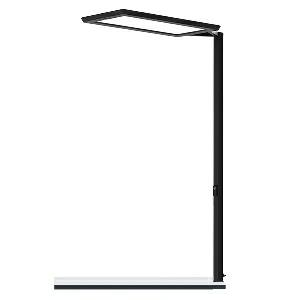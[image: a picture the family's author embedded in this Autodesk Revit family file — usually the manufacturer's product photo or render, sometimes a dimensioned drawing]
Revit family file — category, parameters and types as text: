
# Revit family: yara_single_-_yat_12000_840_r_sw_cee_00_00810197_816a
name_source: partatom
category: Lighting Fixtures
units: mm (PartAtom-declared; Revit-internal decimal feet)

## family parameters
Cut with Voids When Loaded = No
Host = Face
Light Source = No
Part Type = Normal
Room Calculation Point = No
Round Connector Dimension = Use Diameter
Shared = No

## types (1)
- YARA.single - YAT 12000/840/R/SW/CEE/00 (1 x LED, 12000 lm, 4000K)
    Apparent Load = 84 VA
    Approval mark = CE
    CIE Flux Codes = 58 87 97 13 100
    Color Rendering = 80-89
    Color Temperature = 4000K
    Control Gear = Electronic ballast
    Default Elevation = 1800 mm
    Description = YAT 12000/840/R/SW/CEE/00/|Desk-mounted luminaire|light source: LED|work equipment: Electronic ballast DALI|connected load: 220-240 V, 50/60 Hz|Power consumption: approx. 84 W|standby: approx. 0,50|power factor: approx. 0,966|luminous flux: 12000 lm|luminous efficacy: 142 lm/W|light distribution: Direct/indirect|direct ratio: approx. 13 %|colour temperature: Cold white, ca. 4000 K|color rendering index (CRI): >= 80|chromaticity tolerance:  3 SDCM|technology: Presence and daylight sensor control (PIR)|operation: Wireless switch|luminaire body|material: Aluminium/plastic|surface: Powder coatet|colour: Black|lamp cover: Acrylic (PMMA), Satine, Structured|tubular section|material: Steel tube|surface: Powder-coated|Form: Tubular section upright|colour of tubular section: Black|weight (net): approx. 7.7 kg|mains lead: 3.00 m Mains plug CEE 7/VII|Fastening: Socket, Table adaptor|glare control: Prism aperture|luminance(L65): <= 2200 cd/m|unified glare rating(4H 8H): <=  16|special features: App control, Asymmetric radiation, Direct and indirect lighting component with edge light and light guidetechnology for a homogeneous light exit, Flicker-free, Magnetic control panel, freely positionable, PIR movement and daylight sensor|Approval mark: VDE - ENEC|
    Frequency = 50 Hz, 60 Hz
    Height = 24 mm  [stored 0.0787402 ft]
    Lamp = 1 x LED
    Lamp Light Flux = 12000 lm
    Lamp count = 1
    Length = 690 mm
    Luminous efficacy = 143 lm/W
    Manufacturer = Waldmann
    ModVariant = No
    Model = 00810197
    Mounting Place = Table
    Mounting Type = Surface mounted
    Number of Poles = 1
    OnlyDefault = Yes
    Power Factor = 1
    Product Name = YARA.single - YAT 12000/840/R/SW/CEE/00
    Product group = Desk mounted luminaire
    ProductGroupID = 22
    Protection Class = Protection class I
    Protection Degree = IP 20
    RLX_Detail_Level = 1
    RLX_Emergency_Light_Flux = 0 lm
    RLX_Emergency_Type = 0
    RLX_Emergency_Type_DB = No
    RlxData = <blob elided: 61981 chars, md5=826b55bd>
    Socket = socket
    Standby Power = 0 W
    System Light Flux = 12000 lm
    System Power = 84 W
    Type Comments = Product without accessories
    Type Image = yat-r-sw.jpg
    URL = http://relux.com
    VarID = ---
    Voltage = 230 V
    Voltage Range = 220-240 V
    Weight = 0.00 kg
    Width = 358 mm

note: [stored X ft] marks values corroborated as IEEE doubles in the binary element streams (Revit-internal decimal feet)

## geometry (parser evidence)
native form markers: Blend x4, Sweep x15
no freeform markers — native parametric forms only
